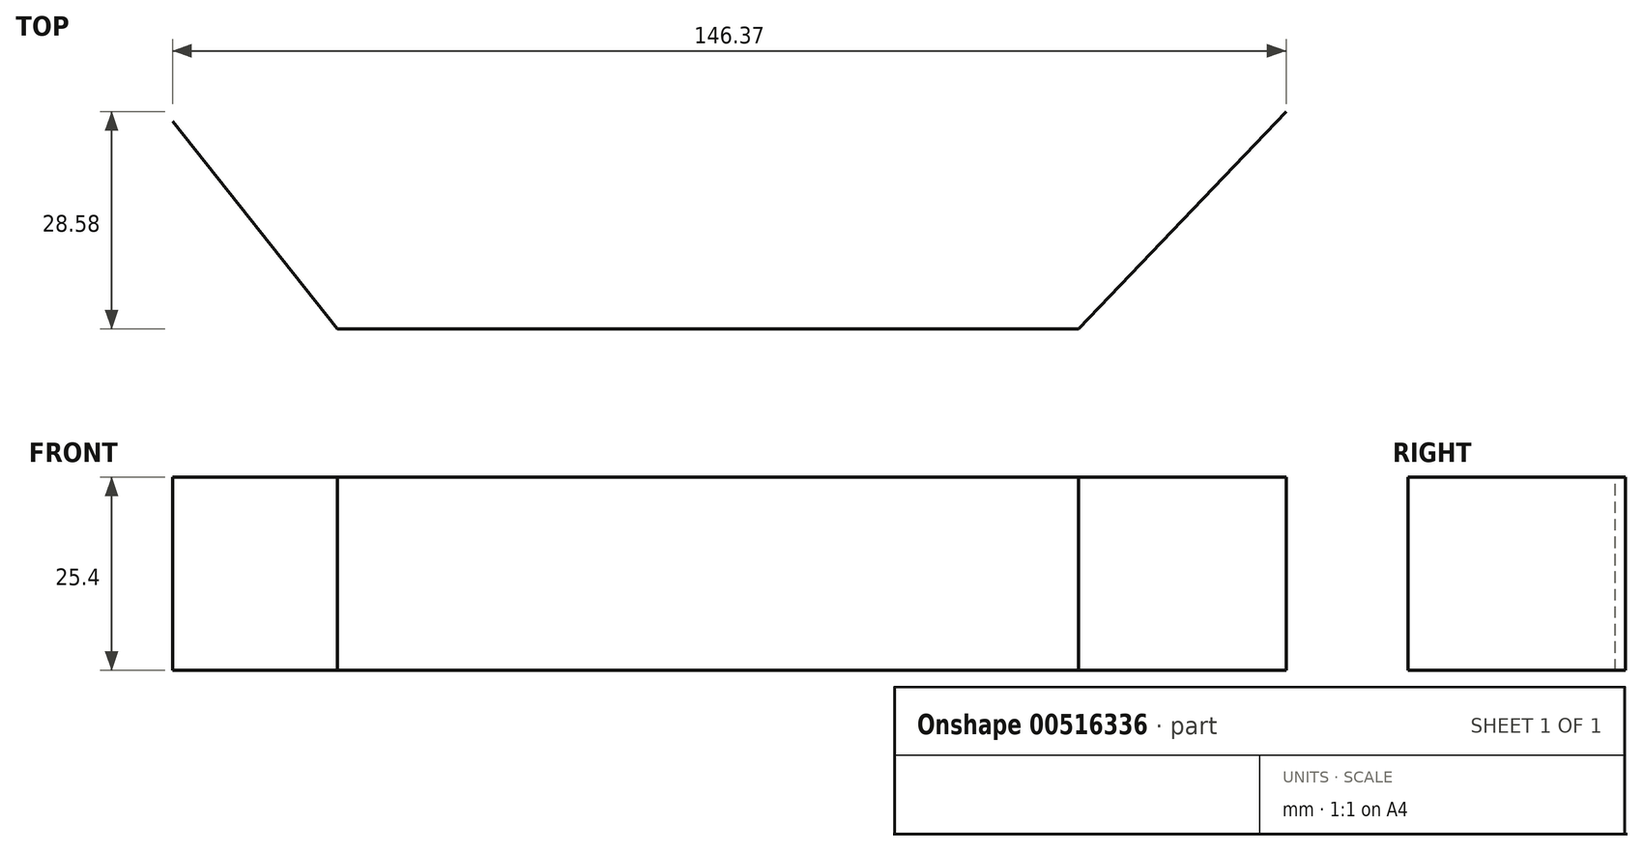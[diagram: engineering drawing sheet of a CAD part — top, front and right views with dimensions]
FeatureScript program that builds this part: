
annotation { "Feature Type Name" : "Feature", "Feature Type Description" : "" }
export const myFeature = defineFeature(function(context is Context, id is Id, definition is map)
    precondition{}
    {
        {
            var Q0;
            Q0=qCreatedBy(makeId("Top.planeOp"),FACE);
            var sketch = newSketch(context, id + "F0", { "sketchPlane" : qUnion([Q0])});
            skLineSegment(sketch, "E0", {"start": v(-72.32, 27.28) * mm, "end": v(-50.67, 0) * mm});
            skLineSegment(sketch, "E1", {"start": v(-50.67, 0) * mm, "end": v(46.77, 0) * mm});
            skLineSegment(sketch, "E2", {"start": v(46.77, 0) * mm, "end": v(74.05, 28.58) * mm});
            skSolve(sketch);
        }
        {
            var Q0;
            Q0=sQuery(id+"F0.wireOp",EDGE,"E2");
            var Q1;
            Q1=sQuery(id+"F0.wireOp",EDGE,"E1");
            var Q2;
            Q2=sQuery(id+"F0.wireOp",EDGE,"E0");
            extrude(context, id + "F1", {"bodyType" : ToolBodyType.SURFACE, "surfaceEntities" : qUnion([Q0, Q1, Q2]), "depth" : 25.4 * mm, "offsetDistance" : 25.4 * mm});
        }
    });
